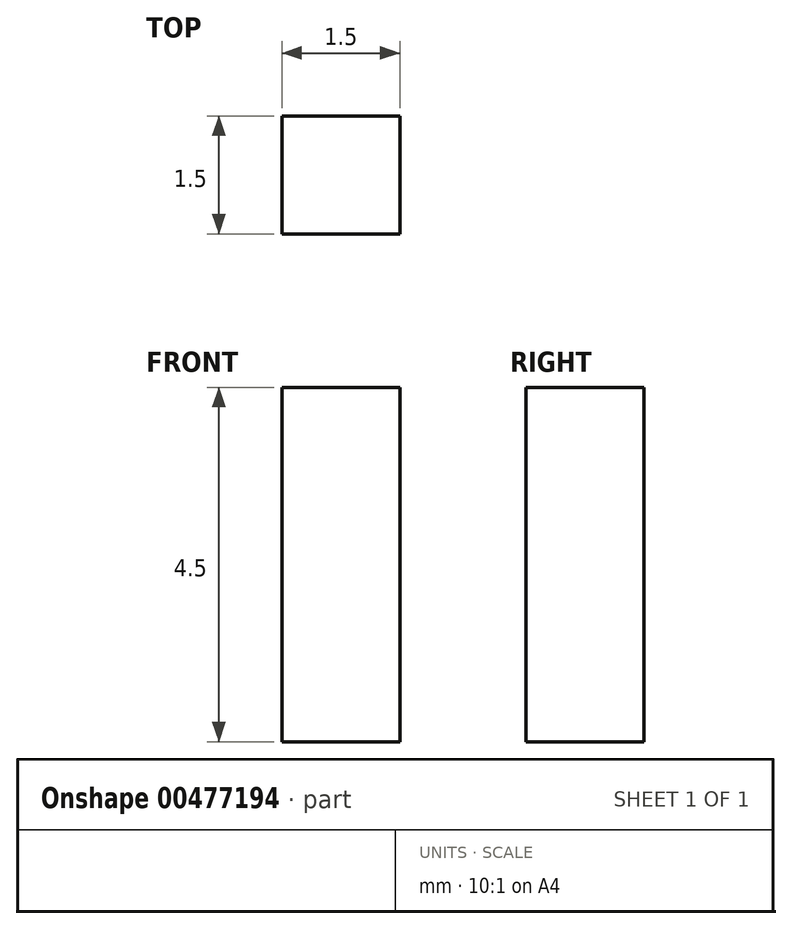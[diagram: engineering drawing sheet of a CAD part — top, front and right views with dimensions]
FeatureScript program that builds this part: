
annotation { "Feature Type Name" : "Feature", "Feature Type Description" : "" }
export const myFeature = defineFeature(function(context is Context, id is Id, definition is map)
    precondition{}
    {
        {
            var Q0;
            Q0=qCreatedBy(makeId("Top.planeOp"),FACE);
            var sketch = newSketch(context, id + "F0", { "sketchPlane" : qUnion([Q0])});
            skLineSegment(sketch, "E0.bottom", {"start": v(0.75, 0.75) * mm, "end": v(-0.75, 0.75) * mm});
            skLineSegment(sketch, "E0.top", {"start": v(0.75, -0.75) * mm, "end": v(-0.75, -0.75) * mm});
            skLineSegment(sketch, "E0.left", {"start": v(0.75, 0.75) * mm, "end": v(0.75, -0.75) * mm});
            skLineSegment(sketch, "E0.right", {"start": v(-0.75, 0.75) * mm, "end": v(-0.75, -0.75) * mm});
            skPoint(sketch, "E0.middle", {"position": v(0, 0) * mm});
            skSolve(sketch);
        }
        {
            var Q0;
            Q0 = qSketchRegion(id + "F0", true);
            extrude(context, id + "F1", {"entities" : qUnion([Q0]), "depth" : 4.5 * mm});
        }
    });
